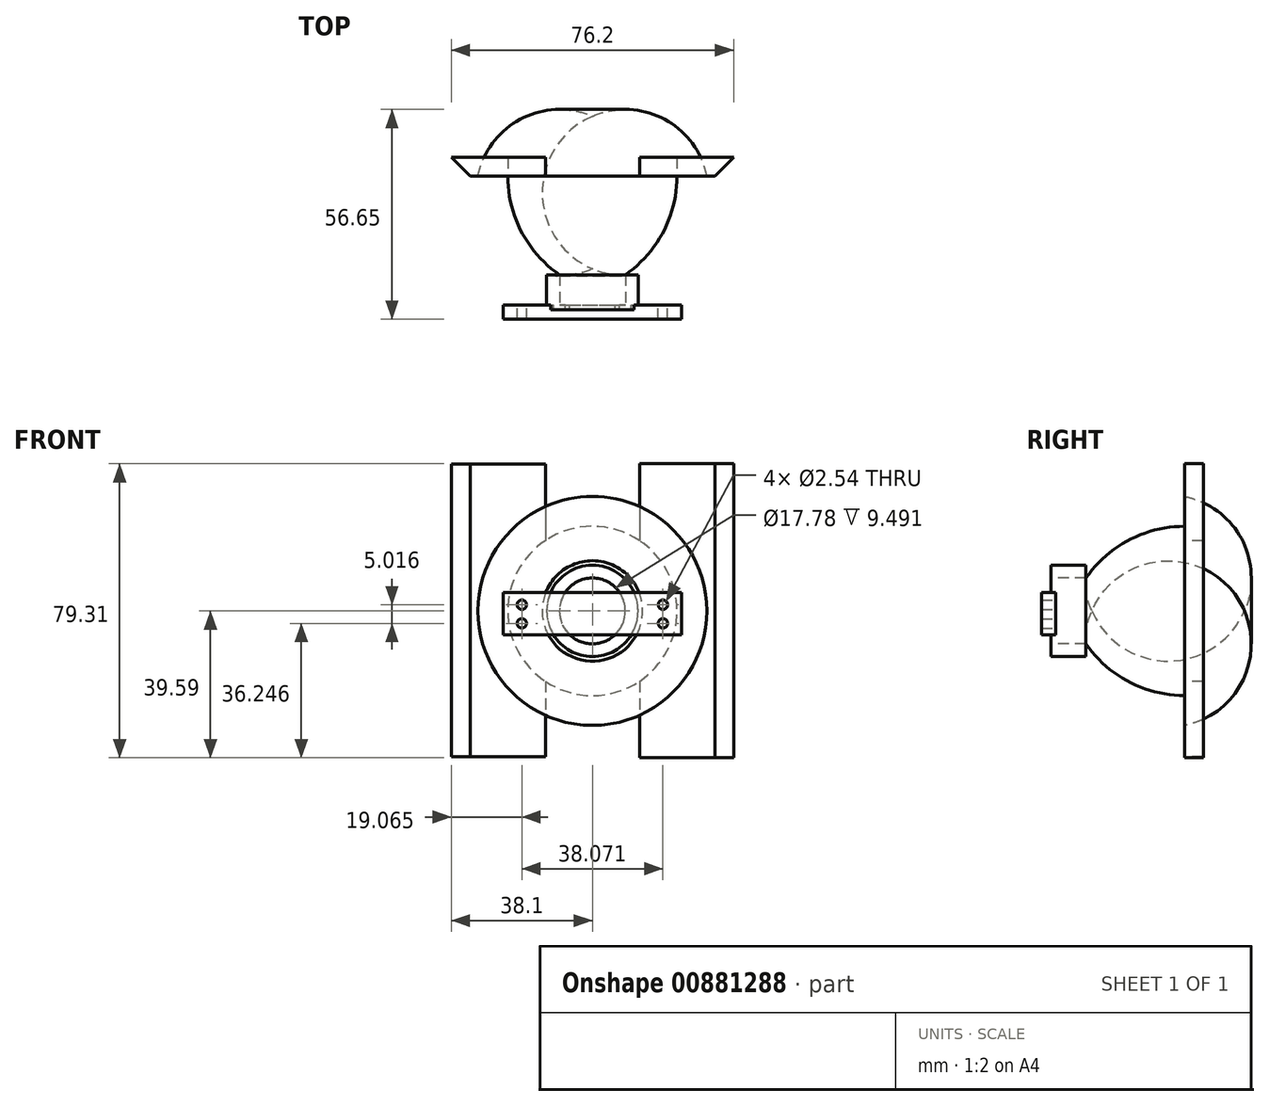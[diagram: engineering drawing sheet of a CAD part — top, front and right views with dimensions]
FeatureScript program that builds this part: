
annotation { "Feature Type Name" : "Feature", "Feature Type Description" : "" }
export const myFeature = defineFeature(function(context is Context, id is Id, definition is map)
    precondition{}
    {
        {
            var Q0;
            Q0=qCreatedBy(makeId("Top.planeOp"),FACE);
            var sketch = newSketch(context, id + "F0", { "sketchPlane" : qUnion([Q0])});
            skLineSegment(sketch, "E0", {"start": v(0, -11.28) * mm, "end": v(0, 40.91) * mm, "construction": true});
            skLineSegment(sketch, "E1", {"start": v(0, 0) * mm, "end": v(12.33, 0) * mm});
            skLineSegment(sketch, "E2", {"start": v(12.33, 0) * mm, "end": v(12.33, 4.59) * mm});
            skLineSegment(sketch, "E3", {"start": v(12.33, 4.59) * mm, "end": v(0, 4.59) * mm});
            skLineSegment(sketch, "E4", {"start": v(0, 4.59) * mm, "end": v(0, 0) * mm});
            skLineSegment(sketch, "E5", {"start": v(12.33, 4.59) * mm, "end": v(12.33, 12.8) * mm});
            skLineSegment(sketch, "E6", {"start": v(8.89, 4.59) * mm, "end": v(8.89, 12.8) * mm});
            skLineSegment(sketch, "E7", {"start": v(22.85, 39.38) * mm, "end": v(30.9, 39.38) * mm});
            skArc(sketch, "E8", {"start": v(8.89, 12.8) * mm, "mid": v(19.13, 24.38) * mm, "end": v(22.85, 39.38) * mm});
            skArc(sketch, "E9", {"start": v(12.33, 12.8) * mm, "mid": v(27.29, 22.13) * mm, "end": v(30.9, 39.38) * mm});
            skLineSegment(sketch, "E10", {"start": v(22.85, 39.38) * mm, "end": v(0, 39.38) * mm, "construction": true});
            skSolve(sketch);
        }
        {
            var Q0;
            {var subQ1=sQuery(id+"F0.wireOp",EDGE,"E5");Q0=makeQuery(id+"F0.imprint","IMPRINT",FACE,{"disambiguationData":[TD([[makeQuery(id+"F0.imprint","IMPRINT",EDGE,{"derivedFrom":subQ1}),1.0]])]});}
            var Q1;
            Q1=sQuery(id+"F0.wireOp",EDGE,"E0");
            revolve(context, id + "F1", {"surfaceOperationType" : NewSurfaceOperationType.NEW, "entities" : qUnion([Q0]), "axis" : qUnion([Q1]), "revolveType" : RevolveType.FULL});
        }
        {
            var Q0;
            Q0=makeQuery(id+"F1.opRevolve","SWEPT_FACE",FACE,{"disambiguationData":[OSD([sQuery(id+"F0.wireOp",EDGE,"E7")])]});
            var sketch = newSketch(context, id + "F2", { "sketchPlane" : qUnion([Q0])});
            skLineSegment(sketch, "E11.bottom", {"start": v(12.7, 39.61) * mm, "end": v(38.1, 39.61) * mm});
            skLineSegment(sketch, "E11.top", {"start": v(12.7, -39.37) * mm, "end": v(38.1, -39.37) * mm});
            skLineSegment(sketch, "E11.left", {"start": v(12.7, 39.61) * mm, "end": v(12.7, -39.37) * mm});
            skLineSegment(sketch, "E11.right", {"start": v(38.1, 39.61) * mm, "end": v(38.1, -39.37) * mm});
            skLineSegment(sketch, "E12.bottom", {"start": v(-38.1, 39.72) * mm, "end": v(-12.7, 39.72) * mm});
            skLineSegment(sketch, "E12.top", {"start": v(-38.1, -39.6) * mm, "end": v(-12.7, -39.6) * mm});
            skLineSegment(sketch, "E12.left", {"start": v(-38.1, 39.72) * mm, "end": v(-38.1, -39.6) * mm});
            skLineSegment(sketch, "E12.right", {"start": v(-12.7, 39.72) * mm, "end": v(-12.7, -39.6) * mm});
            skSolve(sketch);
        }
        {
            var Q0;
            {var subQ1=sQuery(id+"F2.wireOp",EDGE,"E12.bottom");Q0=makeQuery(id+"F2.imprint","IMPRINT",FACE,{"disambiguationData":[TD([[makeQuery(id+"F2.imprint","IMPRINT",EDGE,{"derivedFrom":subQ1}),-1.0]])]});}
            var Q1;
            {var subQ0=sQuery(id+"F2.wireOp",EDGE,"E12.right");var subQ1=sQuery(id+"F0.wireOp",EDGE,"E7");var subQ2=makeQuery(id+"F1.opRevolve","SWEPT_EDGE",EDGE,{"disambiguationData":[OSD([subQ1,sQuery(id+"F0.wireOp",EDGE,"E9")])]});var subQ3=makeQuery(id+"F2.imprint","INTERSECT",VERTEX,{"disambiguationData":[OD(0.0)],"derivedFrom":[subQ2,subQ0]});Q1=makeQuery(id+"F2.imprint","IMPRINT",FACE,{"disambiguationData":[TD([[makeQuery(id+"F2.imprint","IMPRINT",EDGE,{"disambiguationData":[TD([[subQ3,-1.0]])],"derivedFrom":subQ0}),-1.0]])]});}
            var Q2;
            {var subQ1=sQuery(id+"F2.wireOp",EDGE,"E11.bottom");Q2=makeQuery(id+"F2.imprint","IMPRINT",FACE,{"disambiguationData":[TD([[makeQuery(id+"F2.imprint","IMPRINT",EDGE,{"derivedFrom":subQ1}),-1.0]])]});}
            var Q3;
            {var subQ0=sQuery(id+"F2.wireOp",EDGE,"E11.left");var subQ1=sQuery(id+"F0.wireOp",EDGE,"E7");var subQ2=makeQuery(id+"F1.opRevolve","SWEPT_EDGE",EDGE,{"disambiguationData":[OSD([subQ1,sQuery(id+"F0.wireOp",EDGE,"E9")])]});var subQ3=makeQuery(id+"F2.imprint","INTERSECT",VERTEX,{"disambiguationData":[OD(0.0)],"derivedFrom":[subQ2,subQ0]});Q3=makeQuery(id+"F2.imprint","IMPRINT",FACE,{"disambiguationData":[TD([[makeQuery(id+"F2.imprint","IMPRINT",EDGE,{"disambiguationData":[TD([[subQ3,-1.0]])],"derivedFrom":subQ0}),1.0]])]});}
            extrude(context, id + "F3", {"entities" : qUnion([Q0, Q1, Q2, Q3]), "operationType" : NewBodyOperationType.ADD, "depth" : 5.08 * mm, "offsetDistance" : 25.4 * mm});
        }
        {
            var Q0;
            Q0=makeQuery(id+"F1.opRevolve","SWEPT_FACE",FACE,{"disambiguationData":[OSD([sQuery(id+"F0.wireOp",EDGE,"E3")])]});
            var sketch = newSketch(context, id + "F4", { "sketchPlane" : qUnion([Q0])});
            skLineSegment(sketch, "E13.bottom", {"start": v(-24.12, 5.02) * mm, "end": v(24.12, 5.02) * mm});
            skLineSegment(sketch, "E13.top", {"start": v(-24.12, -6.4) * mm, "end": v(24.12, -6.4) * mm});
            skLineSegment(sketch, "E13.left", {"start": v(-24.12, 5.02) * mm, "end": v(-24.12, -6.4) * mm});
            skLineSegment(sketch, "E13.right", {"start": v(24.12, 5.02) * mm, "end": v(24.12, -6.4) * mm});
            skPoint(sketch, "E13.middle", {"position": v(0, -0.7) * mm});
            skPoint(sketch, "E14", {"position": v(-19.04, 1.67) * mm});
            skPoint(sketch, "E15", {"position": v(19.04, 1.67) * mm});
            skPoint(sketch, "E16", {"position": v(-19.04, -3.34) * mm});
            skPoint(sketch, "E17", {"position": v(19.04, -3.34) * mm});
            skSolve(sketch);
        }
        {
            var Q0;
            Q0 = qSketchRegion(id + "F4", true);
            extrude(context, id + "F5", {"entities" : qUnion([Q0]), "operationType" : NewBodyOperationType.ADD, "depth" : 3.8 * mm, "offsetDistance" : 25.4 * mm});
        }
        {
            var Q0;
            Q0=sQuery(id+"F4.wireOp",VERTEX,"E14");
            var Q1;
            Q1=makeQuery(id+"F1.opRevolve","SWEPT_BODY",BODY,{"disambiguationData":[OSD([sQuery(id+"F0.wireOp",EDGE,"E3"),sQuery(id+"F0.wireOp",EDGE,"E5"),sQuery(id+"F0.wireOp",EDGE,"E6"),sQuery(id+"F0.wireOp",EDGE,"E7"),sQuery(id+"F0.wireOp",EDGE,"E8"),sQuery(id+"F0.wireOp",EDGE,"E9")])]});
            hole(context, id + "F6", {"style" : HoleStyle.SIMPLE, "endStyle" : HoleEndStyle.THROUGH, "oppositeDirection" : true, "holeDiameter" : 2.54 * mm, "majorDiameter" : 6.35 * mm, "isTappedThrough" : true, "tappedDepth" : 12.7 * mm, "tapClearance" : 3, "locations" : qUnion([Q0]), "scope" : qUnion([Q1])});
        }
        {
            var Q0;
            Q0=sQuery(id+"F4.wireOp",VERTEX,"E16");
            var Q1;
            Q1=makeQuery(id+"F1.opRevolve","SWEPT_BODY",BODY,{"disambiguationData":[OSD([sQuery(id+"F0.wireOp",EDGE,"E3"),sQuery(id+"F0.wireOp",EDGE,"E5"),sQuery(id+"F0.wireOp",EDGE,"E6"),sQuery(id+"F0.wireOp",EDGE,"E7"),sQuery(id+"F0.wireOp",EDGE,"E8"),sQuery(id+"F0.wireOp",EDGE,"E9")])]});
            hole(context, id + "F7", {"style" : HoleStyle.SIMPLE, "endStyle" : HoleEndStyle.THROUGH, "oppositeDirection" : true, "holeDiameter" : 2.54 * mm, "majorDiameter" : 6.35 * mm, "isTappedThrough" : true, "tappedDepth" : 12.7 * mm, "tapClearance" : 3, "locations" : qUnion([Q0]), "scope" : qUnion([Q1])});
        }
        {
            var Q0;
            Q0=sQuery(id+"F4.wireOp",VERTEX,"E17");
            var Q1;
            Q1=makeQuery(id+"F1.opRevolve","SWEPT_BODY",BODY,{"disambiguationData":[OSD([sQuery(id+"F0.wireOp",EDGE,"E3"),sQuery(id+"F0.wireOp",EDGE,"E5"),sQuery(id+"F0.wireOp",EDGE,"E6"),sQuery(id+"F0.wireOp",EDGE,"E7"),sQuery(id+"F0.wireOp",EDGE,"E8"),sQuery(id+"F0.wireOp",EDGE,"E9")])]});
            hole(context, id + "F8", {"style" : HoleStyle.SIMPLE, "endStyle" : HoleEndStyle.THROUGH, "oppositeDirection" : true, "holeDiameter" : 2.54 * mm, "majorDiameter" : 6.35 * mm, "isTappedThrough" : true, "tappedDepth" : 12.7 * mm, "tapClearance" : 3, "locations" : qUnion([Q0]), "scope" : qUnion([Q1])});
        }
        {
            var Q0;
            Q0=sQuery(id+"F4.wireOp",VERTEX,"E15");
            var Q1;
            Q1=makeQuery(id+"F1.opRevolve","SWEPT_BODY",BODY,{"disambiguationData":[OSD([sQuery(id+"F0.wireOp",EDGE,"E3"),sQuery(id+"F0.wireOp",EDGE,"E5"),sQuery(id+"F0.wireOp",EDGE,"E6"),sQuery(id+"F0.wireOp",EDGE,"E7"),sQuery(id+"F0.wireOp",EDGE,"E8"),sQuery(id+"F0.wireOp",EDGE,"E9")])]});
            hole(context, id + "F9", {"style" : HoleStyle.SIMPLE, "endStyle" : HoleEndStyle.THROUGH, "oppositeDirection" : true, "holeDiameter" : 2.54 * mm, "majorDiameter" : 6.35 * mm, "isTappedThrough" : true, "tappedDepth" : 12.7 * mm, "tapClearance" : 3, "locations" : qUnion([Q0]), "scope" : qUnion([Q1])});
        }
        {
            var Q0;
            Q0=makeQuery(id+"F3.opExtrude","CAP_EDGE",EDGE,{"disambiguationData":[OSD([sQuery(id+"F2.wireOp",EDGE,"E11.right")])],"isStart":true});
            chamfer(context, id + "F10", {"entities" : qUnion([Q0]), "width" : 5.08 * mm, "tangentPropagation" : true});
        }
        {
            var Q0;
            Q0=makeQuery(id+"F3.opExtrude","CAP_EDGE",EDGE,{"disambiguationData":[OSD([sQuery(id+"F2.wireOp",EDGE,"E12.left")])],"isStart":true});
            chamfer(context, id + "F11", {"entities" : qUnion([Q0]), "width" : 5.08 * mm, "tangentPropagation" : true});
        }
        {
            var Q0;
            {var subQ0=sQuery(id+"F4.wireOp",EDGE,"E13.top");Q0=makeQuery(id+"F5.boolean.opBoolean","SPLIT",FACE,{"disambiguationData":[TD([makeQuery(id+"F5.opExtrude","SWEPT_FACE",FACE,{"disambiguationData":[OSD([subQ0])]})])],"derivedFrom":makeQuery(id+"F1.opRevolve","SWEPT_FACE",FACE,{"disambiguationData":[OSD([sQuery(id+"F0.wireOp",EDGE,"E3")])]})});}
            extrude(context, id + "F12", {"entities" : qUnion([Q0]), "operationType" : NewBodyOperationType.ADD, "depth" : 1.27 * mm, "offsetDistance" : 25.4 * mm});
        }
        {
            var Q0;
            {var subQ0=sQuery(id+"F4.wireOp",EDGE,"E13.bottom");Q0=makeQuery(id+"F5.boolean.opBoolean","SPLIT",FACE,{"disambiguationData":[TD([makeQuery(id+"F5.opExtrude","SWEPT_FACE",FACE,{"disambiguationData":[OSD([subQ0])]})])],"derivedFrom":makeQuery(id+"F1.opRevolve","SWEPT_FACE",FACE,{"disambiguationData":[OSD([sQuery(id+"F0.wireOp",EDGE,"E3")])]})});}
            extrude(context, id + "F13", {"entities" : qUnion([Q0]), "operationType" : NewBodyOperationType.ADD, "depth" : 1.27 * mm, "offsetDistance" : 25.4 * mm});
        }
    });
